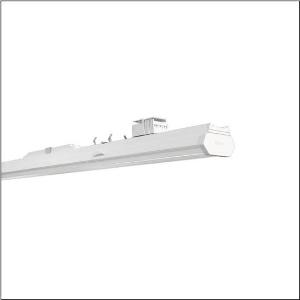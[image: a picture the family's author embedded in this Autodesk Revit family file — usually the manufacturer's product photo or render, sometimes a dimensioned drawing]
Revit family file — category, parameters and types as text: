
# Revit family: licross_r__21_protected_ho_52td12mn4e5m_88f3
name_source: partatom
category: Lighting Fixtures
units: mm (PartAtom-declared; Revit-internal decimal feet)

## family parameters
Cut with Voids When Loaded = No
Host = Face
Light Source = No
Part Type = Normal
Room Calculation Point = No
Round Connector Dimension = Use Diameter
Shared = No

## types (1)
- --- (1 x LED, 14780 lm, 83.2 W, 4000K)
    Apparent Load = 83 VA
    CIE Flux Codes = 70 91 97 98 100
    Color Rendering = 80
    Color Temperature = 4000K
    Default Elevation = 1800 mm
    Description = Licross® 21 Protected HO, luminaire insert, of sheet steel, galvanised, coil coated, white, length: 1.500mm, width: 90mm, height: 101mm, LED rated luminous flux: 14.790lm, light colour: 840, control gear: ON/OFF Multilumen, with plug, 3-pole, with phase selection, mains connection: 220..240V, AC, 50/60Hz, rated input power: 83W, halogen-free wiring, primary light control with lens, of plastic, primary optical cover: cover, of PMMA, light emission: direct distribution, primary light characteristic: symmetric, protection rating (complete): IP54, insulation class (complete): insulation class I (protective earthing), certification: CE, ENEC, VDE, UKCA, protection symbol: D if used in an environment with non-conductive dust loads with corresponding accessories, impact resistance: IK06, permissible ambient temperature for indoor applications: -35..+35°C, corresponds to IFS (International Featured Standards) requirements for safety and quality in the food industry, reducing of maximum allowable ambient temperature of 5°C with ceiling mounting, LABS conformity tested according to VDMA 24364:2018-05, packaging unit: 1 piece
    Height = 92 mm
    Lamp = 1 x LED
    Lamp Light Flux = 14780 lm
    Lamp Power = 83.2 W
    Lamp count = 1
    Length = 1500 mm
    Luminous efficacy = 178 lm/W
    Manufacturer = Siteco
    ModVariant = No
    Model = 52TD12MN4E5M
    Mounting Place = Ceiling
    Mounting Type = Pendant
    Number of Poles = 1
    OnlyDefault = Yes
    Power Factor = 1
    Product Name = Licross® 21 Protected HO
    Product group = luminaire insert
    ProductGroupID = 901
    Protection Class = Protection class I
    Protection Degree = IP 54
    RLX_Detail_Level = 1
    RLX_Emergency_Light_Flux = 0 lm
    RLX_Emergency_Type = 0
    RLX_Emergency_Type_DB = No
    RlxData = <blob elided: 22137 chars, md5=da3699c7>
    Socket = socket
    Standby Power = 0 W
    System Light Flux = 14780 lm
    System Power = 83 W
    Type Comments = factory setting: luminous flux: 100 % | (A | C | E) | 195 mA
    Type Image = l_1256148.jpg
    URL = http://relux.com
    VarID = @adj_039301
    Voltage = 0 V
    Weight = 0.00 kg
    Width = 88 mm

## geometry (parser evidence)
native form markers: Blend x4, Sweep x10
no freeform markers — native parametric forms only
